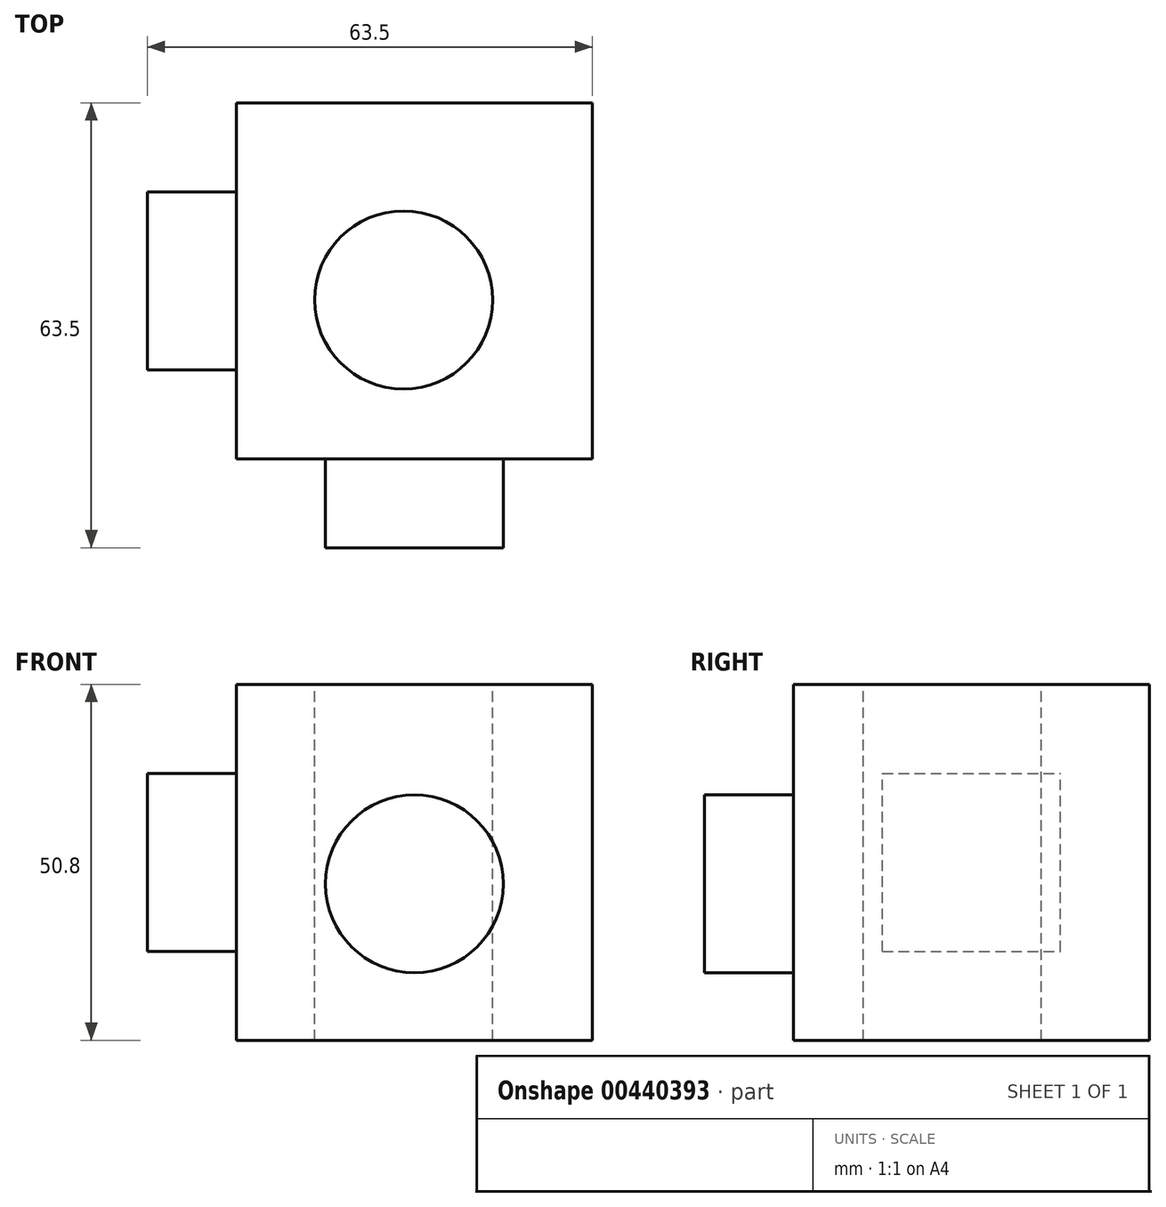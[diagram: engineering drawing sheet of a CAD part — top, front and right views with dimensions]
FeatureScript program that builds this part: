
annotation { "Feature Type Name" : "Feature", "Feature Type Description" : "" }
export const myFeature = defineFeature(function(context is Context, id is Id, definition is map)
    precondition{}
    {
        {
            var Q0;
            Q0=qCreatedBy(makeId("Front.planeOp"),FACE);
            var sketch = newSketch(context, id + "F0", { "sketchPlane" : qUnion([Q0])});
            skLineSegment(sketch, "E0.bottom", {"start": v(0, 0) * mm, "end": v(-50.8, 0) * mm});
            skLineSegment(sketch, "E0.top", {"start": v(0, 50.8) * mm, "end": v(-50.8, 50.8) * mm});
            skLineSegment(sketch, "E0.left", {"start": v(0, 0) * mm, "end": v(0, 50.8) * mm});
            skLineSegment(sketch, "E0.right", {"start": v(-50.8, 0) * mm, "end": v(-50.8, 50.8) * mm});
            skSolve(sketch);
        }
        {
            var Q0;
            Q0 = qSketchRegion(id + "F0", true);
            extrude(context, id + "F1", {"entities" : qUnion([Q0]), "depth" : 50.8 * mm});
        }
        {
            var Q0;
            Q0=makeQuery(id+"F1.opExtrude","CAP_FACE",FACE,{"disambiguationData":[OSD([sQuery(id+"F0.wireOp",EDGE,"E0.bottom"),sQuery(id+"F0.wireOp",EDGE,"E0.top"),sQuery(id+"F0.wireOp",EDGE,"E0.left"),sQuery(id+"F0.wireOp",EDGE,"E0.right")])],"isStart":false});
            var sketch = newSketch(context, id + "F2", { "sketchPlane" : qUnion([Q0])});
            skCircle(sketch, "E1", {"center": v(-25.4, 22.31) * mm, "radius": 12.7 * mm});
            skSolve(sketch);
        }
        {
            var Q0;
            Q0=makeQuery(id+"F2.imprint","IMPRINT",FACE,{"disambiguationData":[TD([[makeQuery(id+"F2.imprint","IMPRINT",EDGE,{"derivedFrom":sQuery(id+"F2.wireOp",EDGE,"E1")}),1.0]])]});
            extrude(context, id + "F3", {"entities" : qUnion([Q0]), "operationType" : NewBodyOperationType.ADD, "depth" : 12.7 * mm});
        }
        {
            var Q0;
            Q0=makeQuery(id+"F1.opExtrude","SWEPT_FACE",FACE,{"disambiguationData":[OSD([sQuery(id+"F0.wireOp",EDGE,"E0.right")])]});
            var sketch = newSketch(context, id + "F4", { "sketchPlane" : qUnion([Q0])});
            skLineSegment(sketch, "E2.bottom", {"start": v(38.1, 12.7) * mm, "end": v(12.7, 12.7) * mm});
            skLineSegment(sketch, "E2.top", {"start": v(38.1, 38.1) * mm, "end": v(12.7, 38.1) * mm});
            skLineSegment(sketch, "E2.left", {"start": v(38.1, 12.7) * mm, "end": v(38.1, 38.1) * mm});
            skLineSegment(sketch, "E2.right", {"start": v(12.7, 12.7) * mm, "end": v(12.7, 38.1) * mm});
            skSolve(sketch);
        }
        {
            var Q0;
            Q0 = qSketchRegion(id + "F4", true);
            extrude(context, id + "F5", {"entities" : qUnion([Q0]), "operationType" : NewBodyOperationType.ADD, "depth" : 12.7 * mm});
        }
        {
            var Q0;
            Q0=makeQuery(id+"F1.opExtrude","SWEPT_FACE",FACE,{"disambiguationData":[OSD([sQuery(id+"F0.wireOp",EDGE,"E0.top")])]});
            var sketch = newSketch(context, id + "F6", { "sketchPlane" : qUnion([Q0])});
            skCircle(sketch, "E3", {"center": v(-26.94, -28.14) * mm, "radius": 12.7 * mm});
            skSolve(sketch);
        }
        {
            var Q0;
            Q0 = qSketchRegion(id + "F6", true);
            extrude(context, id + "F7", {"entities" : qUnion([Q0]), "operationType" : NewBodyOperationType.REMOVE, "oppositeDirection" : true, "depth" : 76.2 * mm});
        }
    });
